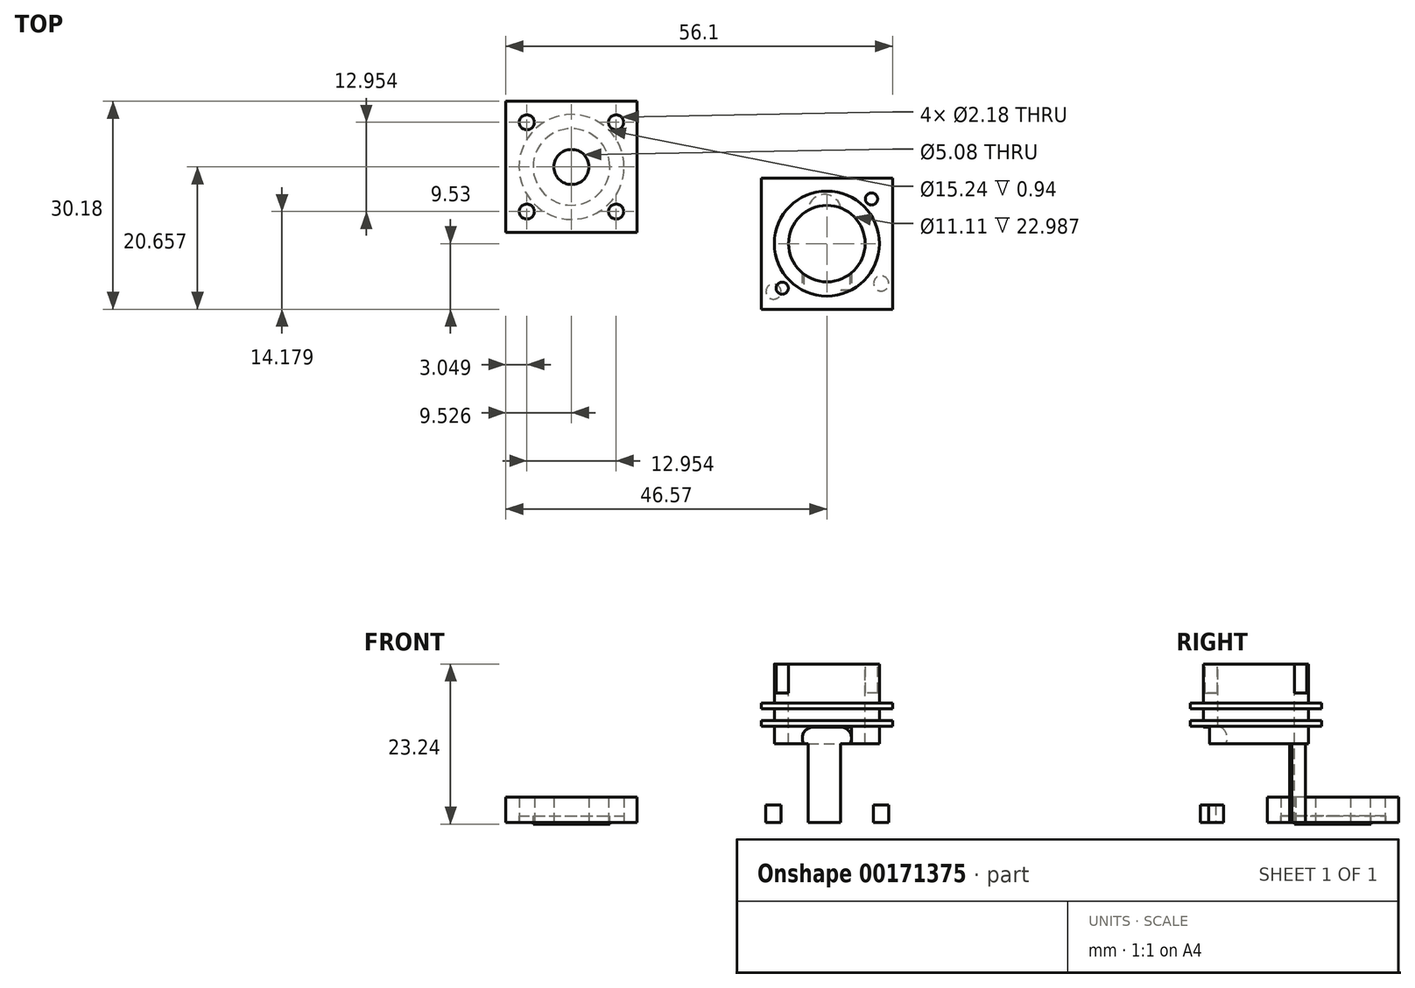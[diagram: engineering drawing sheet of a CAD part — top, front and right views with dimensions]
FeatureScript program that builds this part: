
annotation { "Feature Type Name" : "Feature", "Feature Type Description" : "" }
export const myFeature = defineFeature(function(context is Context, id is Id, definition is map)
    precondition{}
    {
        {
            var Q0;
            Q0=qCreatedBy(makeId("Top.planeOp"),FACE);
            var sketch = newSketch(context, id + "F0", { "sketchPlane" : qUnion([Q0])});
            skLineSegment(sketch, "E0.bottom", {"start": v(9.52, -9.52) * mm, "end": v(-9.53, -9.53) * mm});
            skLineSegment(sketch, "E0.top", {"start": v(9.53, 9.53) * mm, "end": v(-9.53, 9.52) * mm});
            skLineSegment(sketch, "E0.left", {"start": v(9.53, -9.52) * mm, "end": v(9.53, 9.53) * mm});
            skLineSegment(sketch, "E0.right", {"start": v(-9.53, -9.53) * mm, "end": v(-9.53, 9.52) * mm});
            skPoint(sketch, "E0.middle", {"position": v(0, 0) * mm});
            skSolve(sketch);
        }
        {
            var Q0;
            Q0=makeQuery(id+"F0.imprint","IMPRINT",FACE,{"disambiguationData":[TD([[makeQuery(id+"F0.imprint","IMPRINT",EDGE,{"derivedFrom":sQuery(id+"F0.wireOp",EDGE,"E0.bottom")}),-1.0]])]});
            extrude(context, id + "F1", {"entities" : qUnion([Q0]), "depth" : 22.99 * mm});
        }
        {
            var Q0;
            Q0=qCreatedBy(makeId("Front.planeOp"),FACE);
            var sketch = newSketch(context, id + "F2", { "sketchPlane" : qUnion([Q0])});
            skLineSegment(sketch, "E1", {"start": v(-7.62, 2.54) * mm, "end": v(-7.62, 13.97) * mm});
            skLineSegment(sketch, "E2", {"start": v(-7.62, 13.97) * mm, "end": v(-14.19, 13.97) * mm});
            skLineSegment(sketch, "E3", {"start": v(-14.19, 13.97) * mm, "end": v(-14.19, 14.76) * mm});
            skLineSegment(sketch, "E4", {"start": v(-14.19, 14.76) * mm, "end": v(-7.62, 14.76) * mm});
            skLineSegment(sketch, "E5", {"start": v(-7.62, 14.76) * mm, "end": v(-7.62, 16.52) * mm});
            skLineSegment(sketch, "E6", {"start": v(-7.62, 16.52) * mm, "end": v(-14.23, 16.52) * mm});
            skLineSegment(sketch, "E7", {"start": v(-14.23, 16.52) * mm, "end": v(-14.23, 17.31) * mm});
            skLineSegment(sketch, "E8", {"start": v(-14.23, 17.31) * mm, "end": v(-7.62, 17.31) * mm});
            skLineSegment(sketch, "E9", {"start": v(-7.62, 17.31) * mm, "end": v(-7.62, 18.8) * mm});
            skLineSegment(sketch, "E10", {"start": v(-7.62, 18.8) * mm, "end": v(-14.53, 18.8) * mm});
            skLineSegment(sketch, "E11", {"start": v(-7.62, 2.54) * mm, "end": v(-14.53, 2.54) * mm});
            skLineSegment(sketch, "E12", {"start": v(0, 0) * mm, "end": v(0, 2.83) * mm});
            skLineSegment(sketch, "E13", {"start": v(-14.53, 18.8) * mm, "end": v(-14.53, 2.54) * mm});
            skSolve(sketch);
        }
        {
            var Q0;
            {var subQ0=sQuery(id+"F2.wireOp",EDGE,"E1");Q0=makeQuery(id+"F2.imprint","IMPRINT",FACE,{"disambiguationData":[TD([[makeQuery(id+"F2.imprint","IMPRINT",EDGE,{"derivedFrom":subQ0}),1.0]])]});}
            var Q1;
            {var subQ0=sQuery(id+"F2.wireOp",EDGE,"E5");Q1=makeQuery(id+"F2.imprint","IMPRINT",FACE,{"disambiguationData":[TD([[makeQuery(id+"F2.imprint","IMPRINT",EDGE,{"derivedFrom":subQ0}),1.0]])]});}
            var Q2;
            {var subQ0=sQuery(id+"F2.wireOp",EDGE,"E9");Q2=makeQuery(id+"F2.imprint","IMPRINT",FACE,{"disambiguationData":[TD([[makeQuery(id+"F2.imprint","IMPRINT",EDGE,{"derivedFrom":subQ0}),1.0]])]});}
            var Q3;
            Q3=sQuery(id+"F2.wireOp",EDGE,"E12");
            revolve(context, id + "F3", {"operationType" : NewBodyOperationType.REMOVE, "entities" : qUnion([Q0, Q1, Q2]), "axis" : qUnion([Q3]), "revolveType" : RevolveType.FULL, "oppositeDirection" : true});
        }
        {
            var Q0;
            Q0=makeQuery(id+"F1.opExtrude","CAP_FACE",FACE,{"disambiguationData":[OSD([sQuery(id+"F0.wireOp",EDGE,"E0.bottom"),sQuery(id+"F0.wireOp",EDGE,"E0.top"),sQuery(id+"F0.wireOp",EDGE,"E0.left"),sQuery(id+"F0.wireOp",EDGE,"E0.right")])],"isStart":false});
            var sketch = newSketch(context, id + "F4", { "sketchPlane" : qUnion([Q0])});
            skCircle(sketch, "E14", {"center": v(0, 0) * mm, "radius": 5.56 * mm});
            skCircle(sketch, "E15", {"center": v(0, 0) * mm, "radius": 7.62 * mm});
            skCircle(sketch, "E16", {"center": v(6.48, -6.48) * mm, "radius": 0.89 * mm});
            skCircle(sketch, "E17.MirrorC", {"center": v(-6.48, -6.48) * mm, "radius": 0.89 * mm});
            skCircle(sketch, "E18.MirrorC", {"center": v(-6.48, 6.48) * mm, "radius": 0.89 * mm});
            skCircle(sketch, "E19.MirrorC", {"center": v(6.48, 6.48) * mm, "radius": 0.89 * mm});
            skSolve(sketch);
        }
        {
            var Q0;
            Q0=makeQuery(id+"F4.imprint","IMPRINT",FACE,{"disambiguationData":[TD([[makeQuery(id+"F4.imprint","IMPRINT",EDGE,{"derivedFrom":sQuery(id+"F4.wireOp",EDGE,"E14")}),1.0]])]});
            extrude(context, id + "F5", {"entities" : qUnion([Q0]), "operationType" : NewBodyOperationType.REMOVE, "endBound" : BoundingType.THROUGH_ALL, "oppositeDirection" : true, "depth" : 25.4 * mm});
        }
        {
            var Q0;
            Q0=makeQuery(id+"F4.imprint","IMPRINT",FACE,{"disambiguationData":[TD([[makeQuery(id+"F4.imprint","IMPRINT",EDGE,{"derivedFrom":sQuery(id+"F4.wireOp",EDGE,"E15")}),-1.0]])]});
            extrude(context, id + "F6", {"entities" : qUnion([Q0]), "operationType" : NewBodyOperationType.REMOVE, "oppositeDirection" : true, "depth" : 0.76 * mm});
        }
        {
            var Q0;
            Q0=makeQuery(id+"F1.opExtrude","CAP_FACE",FACE,{"disambiguationData":[OSD([sQuery(id+"F0.wireOp",EDGE,"E0.bottom"),sQuery(id+"F0.wireOp",EDGE,"E0.top"),sQuery(id+"F0.wireOp",EDGE,"E0.left"),sQuery(id+"F0.wireOp",EDGE,"E0.right")])],"isStart":true});
            var sketch = newSketch(context, id + "F7", { "sketchPlane" : qUnion([Q0])});
            skCircle(sketch, "E20", {"center": v(0, 0) * mm, "radius": 7.62 * mm});
            skCircle(sketch, "E21", {"center": v(0.33, -4.75) * mm, "radius": 2.39 * mm});
            skCircle(sketch, "E22.MirrorC", {"center": v(-0.33, -4.75) * mm, "radius": 2.39 * mm});
            skLineSegment(sketch, "E23", {"start": v(-0.33, -7.14) * mm, "end": v(0.33, -7.14) * mm});
            skCircle(sketch, "E24", {"center": v(-7.75, -6.99) * mm, "radius": 1.1 * mm});
            skCircle(sketch, "E25", {"center": v(7.87, -5.8) * mm, "radius": 1.1 * mm});
            skCircle(sketch, "E26.MirrorC", {"center": v(7.87, 5.8) * mm, "radius": 1.1 * mm});
            skCircle(sketch, "E27.MirrorC", {"center": v(-7.75, 6.99) * mm, "radius": 1.1 * mm});
            skSolve(sketch);
        }
        {
            var Q0;
            {var subQ0=sQuery(id+"F7.wireOp",EDGE,"E21");var subQ1=makeQuery(id+"F7.imprint","INTERSECT",VERTEX,{"derivedFrom":[subQ0,sQuery(id+"F7.wireOp",EDGE,"E23")]});Q0=makeQuery(id+"F7.imprint","IMPRINT",FACE,{"disambiguationData":[TD([[makeQuery(id+"F7.imprint","IMPRINT",EDGE,{"disambiguationData":[TD([[subQ1,1.0]])],"derivedFrom":subQ0}),1.0]])]});}
            var Q1;
            {var subQ0=sQuery(id+"F7.wireOp",EDGE,"E22.MirrorC");var subQ5=makeQuery(id+"F7.imprint","INTERSECT",VERTEX,{"derivedFrom":[subQ0,sQuery(id+"F7.wireOp",EDGE,"E23")]});Q1=makeQuery(id+"F7.imprint","IMPRINT",FACE,{"disambiguationData":[TD([[makeQuery(id+"F7.imprint","IMPRINT",EDGE,{"disambiguationData":[TD([[subQ5,1.0]])],"derivedFrom":subQ0}),-1.0]])]});}
            var Q2;
            {var subQ0=sQuery(id+"F7.wireOp",EDGE,"E22.MirrorC");var subQ1=sQuery(id+"F7.wireOp",EDGE,"E21");var subQ2=makeQuery(id+"F7.imprint","INTERSECT",VERTEX,{"disambiguationData":[OD(1.0)],"derivedFrom":[subQ1,subQ0]});Q2=makeQuery(id+"F7.imprint","IMPRINT",FACE,{"disambiguationData":[TD([[makeQuery(id+"F7.imprint","IMPRINT",EDGE,{"disambiguationData":[TD([[subQ2,1.0]])],"derivedFrom":subQ1}),1.0]])]});}
            var Q3;
            {var subQ0=sQuery(id+"F7.wireOp",EDGE,"E23");Q3=makeQuery(id+"F7.imprint","IMPRINT",FACE,{"disambiguationData":[TD([[makeQuery(id+"F7.imprint","IMPRINT",EDGE,{"derivedFrom":subQ0}),1.0]])]});}
            extrude(context, id + "F8", {"entities" : qUnion([Q0, Q1, Q2, Q3]), "operationType" : NewBodyOperationType.REMOVE, "oppositeDirection" : true, "depth" : 11.43 * mm});
        }
        {
            var Q0;
            Q0=makeQuery(id+"F7.imprint","IMPRINT",FACE,{"disambiguationData":[TD([[makeQuery(id+"F7.imprint","IMPRINT",EDGE,{"derivedFrom":sQuery(id+"F7.wireOp",EDGE,"E20")}),-1.0]])]});
            extrude(context, id + "F9", {"entities" : qUnion([Q0]), "operationType" : NewBodyOperationType.REMOVE, "oppositeDirection" : true, "depth" : 0.89 * mm});
        }
        {
            var Q0;
            Q0=makeQuery(id+"F7.imprint","IMPRINT",FACE,{"disambiguationData":[TD([[makeQuery(id+"F7.imprint","IMPRINT",EDGE,{"derivedFrom":sQuery(id+"F7.wireOp",EDGE,"E27.MirrorC")}),-1.0]])]});
            var Q1;
            Q1=makeQuery(id+"F7.imprint","IMPRINT",FACE,{"disambiguationData":[TD([[makeQuery(id+"F7.imprint","IMPRINT",EDGE,{"derivedFrom":sQuery(id+"F7.wireOp",EDGE,"E26.MirrorC")}),-1.0]])]});
            var Q2;
            Q2=makeQuery(id+"F7.imprint","IMPRINT",FACE,{"disambiguationData":[TD([[makeQuery(id+"F7.imprint","IMPRINT",EDGE,{"derivedFrom":sQuery(id+"F7.wireOp",EDGE,"E25")}),1.0]])]});
            var Q3;
            Q3=makeQuery(id+"F7.imprint","IMPRINT",FACE,{"disambiguationData":[TD([[makeQuery(id+"F7.imprint","IMPRINT",EDGE,{"derivedFrom":sQuery(id+"F7.wireOp",EDGE,"E24")}),1.0]])]});
            extrude(context, id + "F10", {"entities" : qUnion([Q0, Q1, Q2, Q3]), "operationType" : NewBodyOperationType.REMOVE, "oppositeDirection" : true, "depth" : 2.54 * mm});
        }
        {
            var Q0;
            {var subQ2=sQuery(id+"F0.wireOp",EDGE,"E0.bottom");Q0=makeQuery(id+"F3.boolean.opBoolean","SPLIT",FACE,{"disambiguationData":[TD([makeQuery(id+"F3.opRevolve","SWEPT_FACE",FACE,{"disambiguationData":[OSD([sQuery(id+"F2.wireOp",EDGE,"E10")])]})])],"derivedFrom":makeQuery(id+"F1.opExtrude","SWEPT_FACE",FACE,{"disambiguationData":[OSD([subQ2])]})});}
            var sketch = newSketch(context, id + "F11", { "sketchPlane" : qUnion([Q0])});
            skArc(sketch, "E28", {"start": v(1.98, 10.66) * mm, "mid": v(3.57, 12.24) * mm, "end": v(1.98, 13.83) * mm});
            skArc(sketch, "E29.MirrorC", {"start": v(-1.98, 10.66) * mm, "mid": v(-3.57, 12.24) * mm, "end": v(-1.98, 13.83) * mm});
            skLineSegment(sketch, "E30.bottom", {"start": v(-3.57, 10.66) * mm, "end": v(3.57, 10.66) * mm});
            skLineSegment(sketch, "E30.top", {"start": v(-3.57, 13.83) * mm, "end": v(3.57, 13.83) * mm});
            skLineSegment(sketch, "E30.left", {"start": v(-3.57, 10.66) * mm, "end": v(-3.57, 13.83) * mm});
            skLineSegment(sketch, "E30.right", {"start": v(3.57, 10.66) * mm, "end": v(3.57, 13.83) * mm});
            skSolve(sketch);
        }
        {
            var Q0;
            {var subQ4=sQuery(id+"F11.wireOp",EDGE,"E30.bottom");var subQ6=sQuery(id+"F11.wireOp",EDGE,"E28");var subQ9=makeQuery(id+"F11.imprint","INTERSECT",VERTEX,{"derivedFrom":[subQ6,subQ4]});Q0=makeQuery(id+"F11.imprint","IMPRINT",FACE,{"disambiguationData":[TD([[makeQuery(id+"F11.imprint","IMPRINT",EDGE,{"disambiguationData":[TD([[subQ9,-1.0]])],"derivedFrom":subQ6}),1.0]])]});}
            extrude(context, id + "F12", {"entities" : qUnion([Q0]), "operationType" : NewBodyOperationType.REMOVE, "oppositeDirection" : true, "depth" : 9.52 * mm});
        }
        {
            var Q0;
            {var subQ0=sQuery(id+"F11.wireOp",EDGE,"E30.bottom");var subQ1=sQuery(id+"F11.wireOp",EDGE,"E28");var subQ2=makeQuery(id+"F11.imprint","INTERSECT",VERTEX,{"derivedFrom":[subQ1,subQ0]});Q0=makeQuery(id+"F11.imprint","IMPRINT",FACE,{"disambiguationData":[TD([[makeQuery(id+"F11.imprint","IMPRINT",EDGE,{"disambiguationData":[TD([[subQ2,-1.0]])],"derivedFrom":subQ1}),-1.0]])]});}
            var Q1;
            {var subQ0=sQuery(id+"F11.wireOp",EDGE,"E30.top");var subQ1=sQuery(id+"F11.wireOp",EDGE,"E28");var subQ2=makeQuery(id+"F11.imprint","INTERSECT",VERTEX,{"derivedFrom":[subQ1,subQ0]});Q1=makeQuery(id+"F11.imprint","IMPRINT",FACE,{"disambiguationData":[TD([[makeQuery(id+"F11.imprint","IMPRINT",EDGE,{"disambiguationData":[TD([[subQ2,1.0]])],"derivedFrom":subQ1}),-1.0]])]});}
            var Q2;
            {var subQ0=sQuery(id+"F11.wireOp",EDGE,"E30.top");var subQ1=sQuery(id+"F11.wireOp",EDGE,"E29.MirrorC");var subQ2=makeQuery(id+"F11.imprint","INTERSECT",VERTEX,{"derivedFrom":[subQ1,subQ0]});Q2=makeQuery(id+"F11.imprint","IMPRINT",FACE,{"disambiguationData":[TD([[makeQuery(id+"F11.imprint","IMPRINT",EDGE,{"disambiguationData":[TD([[subQ2,1.0]])],"derivedFrom":subQ1}),1.0]])]});}
            var Q3;
            {var subQ0=sQuery(id+"F11.wireOp",EDGE,"E30.bottom");var subQ1=sQuery(id+"F11.wireOp",EDGE,"E29.MirrorC");var subQ2=makeQuery(id+"F11.imprint","INTERSECT",VERTEX,{"derivedFrom":[subQ1,subQ0]});Q3=makeQuery(id+"F11.imprint","IMPRINT",FACE,{"disambiguationData":[TD([[makeQuery(id+"F11.imprint","IMPRINT",EDGE,{"disambiguationData":[TD([[subQ2,-1.0]])],"derivedFrom":subQ1}),1.0]])]});}
            extrude(context, id + "F13", {"entities" : qUnion([Q0, Q1, Q2, Q3]), "operationType" : NewBodyOperationType.REMOVE, "oppositeDirection" : true, "depth" : 2.8 * mm});
        }
        {
            var Q0;
            Q0=makeQuery(id+"F4.imprint","IMPRINT",FACE,{"disambiguationData":[TD([[makeQuery(id+"F4.imprint","IMPRINT",EDGE,{"derivedFrom":sQuery(id+"F4.wireOp",EDGE,"E19.MirrorC")}),-1.0]])]});
            var Q1;
            Q1=makeQuery(id+"F4.imprint","IMPRINT",FACE,{"disambiguationData":[TD([[makeQuery(id+"F4.imprint","IMPRINT",EDGE,{"derivedFrom":sQuery(id+"F4.wireOp",EDGE,"E16")}),1.0]])]});
            var Q2;
            Q2=makeQuery(id+"F4.imprint","IMPRINT",FACE,{"disambiguationData":[TD([[makeQuery(id+"F4.imprint","IMPRINT",EDGE,{"derivedFrom":sQuery(id+"F4.wireOp",EDGE,"E17.MirrorC")}),-1.0]])]});
            var Q3;
            Q3=makeQuery(id+"F4.imprint","IMPRINT",FACE,{"disambiguationData":[TD([[makeQuery(id+"F4.imprint","IMPRINT",EDGE,{"derivedFrom":sQuery(id+"F4.wireOp",EDGE,"E18.MirrorC")}),1.0]])]});
            extrude(context, id + "F14", {"entities" : qUnion([Q0, Q1, Q2, Q3]), "operationType" : NewBodyOperationType.REMOVE, "oppositeDirection" : true, "depth" : 4.44 * mm});
        }
        {
            var Q0;
            Q0=qCreatedBy(makeId("Top.planeOp"),FACE);
            var sketch = newSketch(context, id + "F15", { "sketchPlane" : qUnion([Q0])});
            skLineSegment(sketch, "E31.bottom", {"start": v(-46.57, 20.65) * mm, "end": v(-27.52, 20.65) * mm});
            skLineSegment(sketch, "E31.top", {"start": v(-46.57, 1.6) * mm, "end": v(-27.52, 1.6) * mm});
            skLineSegment(sketch, "E31.left", {"start": v(-46.57, 20.65) * mm, "end": v(-46.57, 1.6) * mm});
            skLineSegment(sketch, "E31.right", {"start": v(-27.52, 20.65) * mm, "end": v(-27.52, 1.6) * mm});
            skCircle(sketch, "E32", {"center": v(-37.04, 11.13) * mm, "radius": 2.54 * mm});
            skPoint(sketch, "E32.centerSnap0", {"position": v(-46.57, 11.13) * mm});
            skPoint(sketch, "E32.centerSnap1", {"position": v(-37.04, 20.65) * mm});
            skCircle(sketch, "E33", {"center": v(-43.52, 17.6) * mm, "radius": 1.1 * mm});
            skCircle(sketch, "E34.0.1.0", {"center": v(-43.52, 4.65) * mm, "radius": 1.1 * mm});
            skCircle(sketch, "E34.1.0.0", {"center": v(-30.57, 17.6) * mm, "radius": 1.1 * mm});
            skCircle(sketch, "E34.1.1.0", {"center": v(-30.57, 4.65) * mm, "radius": 1.1 * mm});
            skLineSegment(sketch, "E34.direction1", {"start": v(-43.52, 17.6) * mm, "end": v(-30.57, 17.6) * mm, "construction": true});
            skLineSegment(sketch, "E34.direction2", {"start": v(-43.52, 17.6) * mm, "end": v(-43.52, 4.65) * mm, "construction": true});
            skSolve(sketch);
        }
        {
            var Q0;
            Q0=makeQuery(id+"F15.imprint","IMPRINT",FACE,{"disambiguationData":[TD([[makeQuery(id+"F15.imprint","IMPRINT",EDGE,{"derivedFrom":sQuery(id+"F15.wireOp",EDGE,"E31.bottom")}),-1.0]])]});
            extrude(context, id + "F16", {"entities" : qUnion([Q0]), "depth" : 3.66 * mm});
        }
        {
            var Q0;
            Q0=makeQuery(id+"F16.opExtrude","CAP_FACE",FACE,{"disambiguationData":[OSD([sQuery(id+"F15.wireOp",EDGE,"E31.bottom"),sQuery(id+"F15.wireOp",EDGE,"E31.top"),sQuery(id+"F15.wireOp",EDGE,"E31.left"),sQuery(id+"F15.wireOp",EDGE,"E31.right"),sQuery(id+"F15.wireOp",EDGE,"E32"),sQuery(id+"F15.wireOp",EDGE,"E33"),sQuery(id+"F15.wireOp",EDGE,"E34.0.1.0"),sQuery(id+"F15.wireOp",EDGE,"E34.1.0.0"),sQuery(id+"F15.wireOp",EDGE,"E34.1.1.0")])],"isStart":true});
            var sketch = newSketch(context, id + "F17", { "sketchPlane" : qUnion([Q0])});
            skCircle(sketch, "E35", {"center": v(-37.04, -11.13) * mm, "radius": 5.56 * mm});
            skCircle(sketch, "E36", {"center": v(-37.04, -11.13) * mm, "radius": 7.62 * mm});
            skSolve(sketch);
        }
        {
            var Q0;
            Q0=makeQuery(id+"F17.imprint","IMPRINT",FACE,{"disambiguationData":[TD([[makeQuery(id+"F17.imprint","IMPRINT",EDGE,{"derivedFrom":sQuery(id+"F17.wireOp",EDGE,"E35")}),1.0]])]});
            extrude(context, id + "F18", {"entities" : qUnion([Q0]), "operationType" : NewBodyOperationType.ADD, "depth" : 0.25 * mm});
        }
        {
            var Q0;
            Q0=makeQuery(id+"F17.imprint","IMPRINT",FACE,{"disambiguationData":[TD([[makeQuery(id+"F17.imprint","IMPRINT",EDGE,{"derivedFrom":sQuery(id+"F17.wireOp",EDGE,"E35")}),-1.0]])]});
            extrude(context, id + "F19", {"entities" : qUnion([Q0]), "operationType" : NewBodyOperationType.REMOVE, "oppositeDirection" : true, "depth" : 0.94 * mm});
        }
    });
